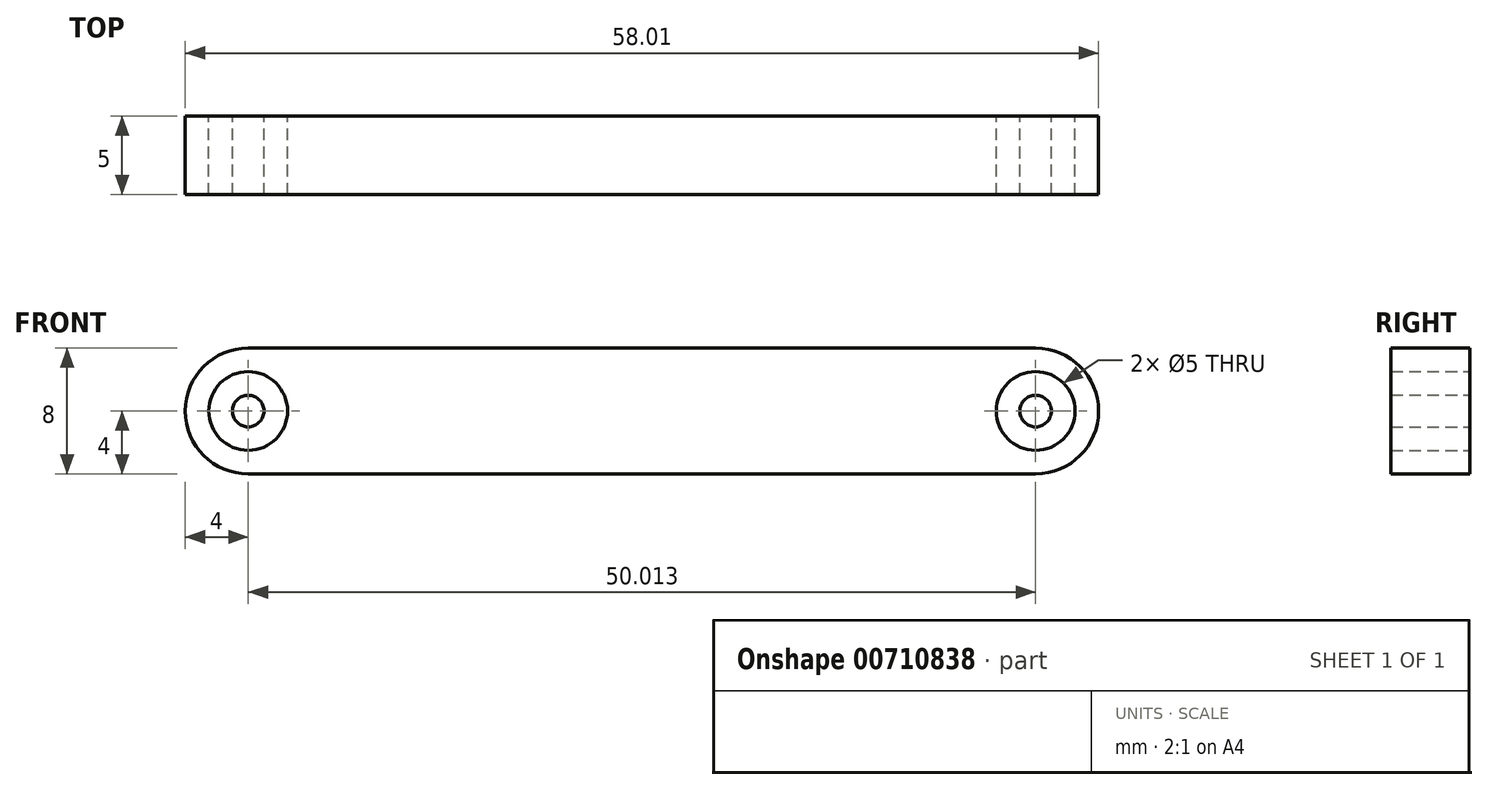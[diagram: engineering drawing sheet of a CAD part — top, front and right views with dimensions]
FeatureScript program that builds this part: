
annotation { "Feature Type Name" : "Feature", "Feature Type Description" : "" }
export const myFeature = defineFeature(function(context is Context, id is Id, definition is map)
    precondition{}
    {
        {
            var Q0;
            Q0=qCreatedBy(makeId("Front.planeOp"),FACE);
            var sketch = newSketch(context, id + "F0", { "sketchPlane" : qUnion([Q0])});
            skCircle(sketch, "E0", {"center": v(0, 0) * mm, "radius": 1 * mm});
            skCircle(sketch, "E1", {"center": v(0, 0) * mm, "radius": 2.5 * mm});
            skArc(sketch, "E2", {"start": v(0, 4) * mm, "mid": v(-4, 0) * mm, "end": v(0, -4) * mm});
            skCircle(sketch, "E3", {"center": v(50.01, 0) * mm, "radius": 1 * mm});
            skCircle(sketch, "E4", {"center": v(50.01, 0) * mm, "radius": 2.5 * mm});
            skArc(sketch, "E5", {"start": v(50.01, -4) * mm, "mid": v(54.01, 0) * mm, "end": v(50.01, 4) * mm});
            skLineSegment(sketch, "E6", {"start": v(0, 4) * mm, "end": v(50.01, 4) * mm});
            skLineSegment(sketch, "E7", {"start": v(0, -4) * mm, "end": v(50.01, -4) * mm});
            skSolve(sketch);
        }
        {
            var Q0;
            Q0=makeQuery(id+"F0.imprint","IMPRINT",FACE,{"disambiguationData":[TD([[makeQuery(id+"F0.imprint","IMPRINT",EDGE,{"derivedFrom":sQuery(id+"F0.wireOp",EDGE,"E1")}),-1.0]])]});
            var Q1;
            Q1=makeQuery(id+"F0.imprint","IMPRINT",FACE,{"disambiguationData":[TD([[makeQuery(id+"F0.imprint","IMPRINT",EDGE,{"derivedFrom":sQuery(id+"F0.wireOp",EDGE,"E0")}),1.0]])]});
            var Q2;
            Q2=makeQuery(id+"F0.imprint","IMPRINT",FACE,{"disambiguationData":[TD([[makeQuery(id+"F0.imprint","IMPRINT",EDGE,{"derivedFrom":sQuery(id+"F0.wireOp",EDGE,"E3")}),1.0]])]});
            extrude(context, id + "F1", {"entities" : qUnion([Q0, Q1, Q2]), "depth" : 5 * mm, "offsetDistance" : 25.4 * mm});
        }
    });
